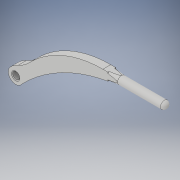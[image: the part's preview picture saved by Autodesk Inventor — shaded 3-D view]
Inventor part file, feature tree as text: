
AUTODESK INVENTOR PART (.ipt)
format: ipt  version: 2018.3 (Build 223284000, 284)  size: 166,912 bytes
history: native  units: in
note: dims shown in document units (in); Inventor stores cm internally (conversion verified against a paired STEP export)
features: sketch x2, extrude x2, revolve x1, plane x1, chamfer x1
ambient origin geometry x8: Origin, YZ Plane, XZ Plane, XY Plane, X Axis, Y Axis, Z Axis, Center Point
bodies: Solid1 (feature_tree)
feature tree (7):
  sketch  "Sketch1"  dims[d0=0.096in d1=0.2in]
  extrude  "Extrusion1"  Depth=0.2in
  revolve  "Revolution1"  [1 undecoded]
  plane  "Work Plane1"
  extrude  "Extrusion2"  Depth=0.107in
  chamfer  "Chamfer1"  Distance=4.268in
  sketch  "Sketch2"  dims[d2=0.6in d3=0.15in d4=2.79in d5=1.186in d6=4.268in d7=1.618in d8=0.812in d9=0.113in d10=0.618in d11=2.015in d12=0.63in d13=0.107in d14=0.108in d17=0.107in d18=0.0in d19=0.13in d20=90.0deg d21=0.0in d22=0.13in d23=-0.0344in d24=0.13in d25=0.13in d26=0.009in d27=0.125in d28=45.0deg]
note: 1 required parameter value undecoded (feature->parameter linkage not recoverable at this tier; creation-order binding heuristic only, values carry confidence <= 0.55)
